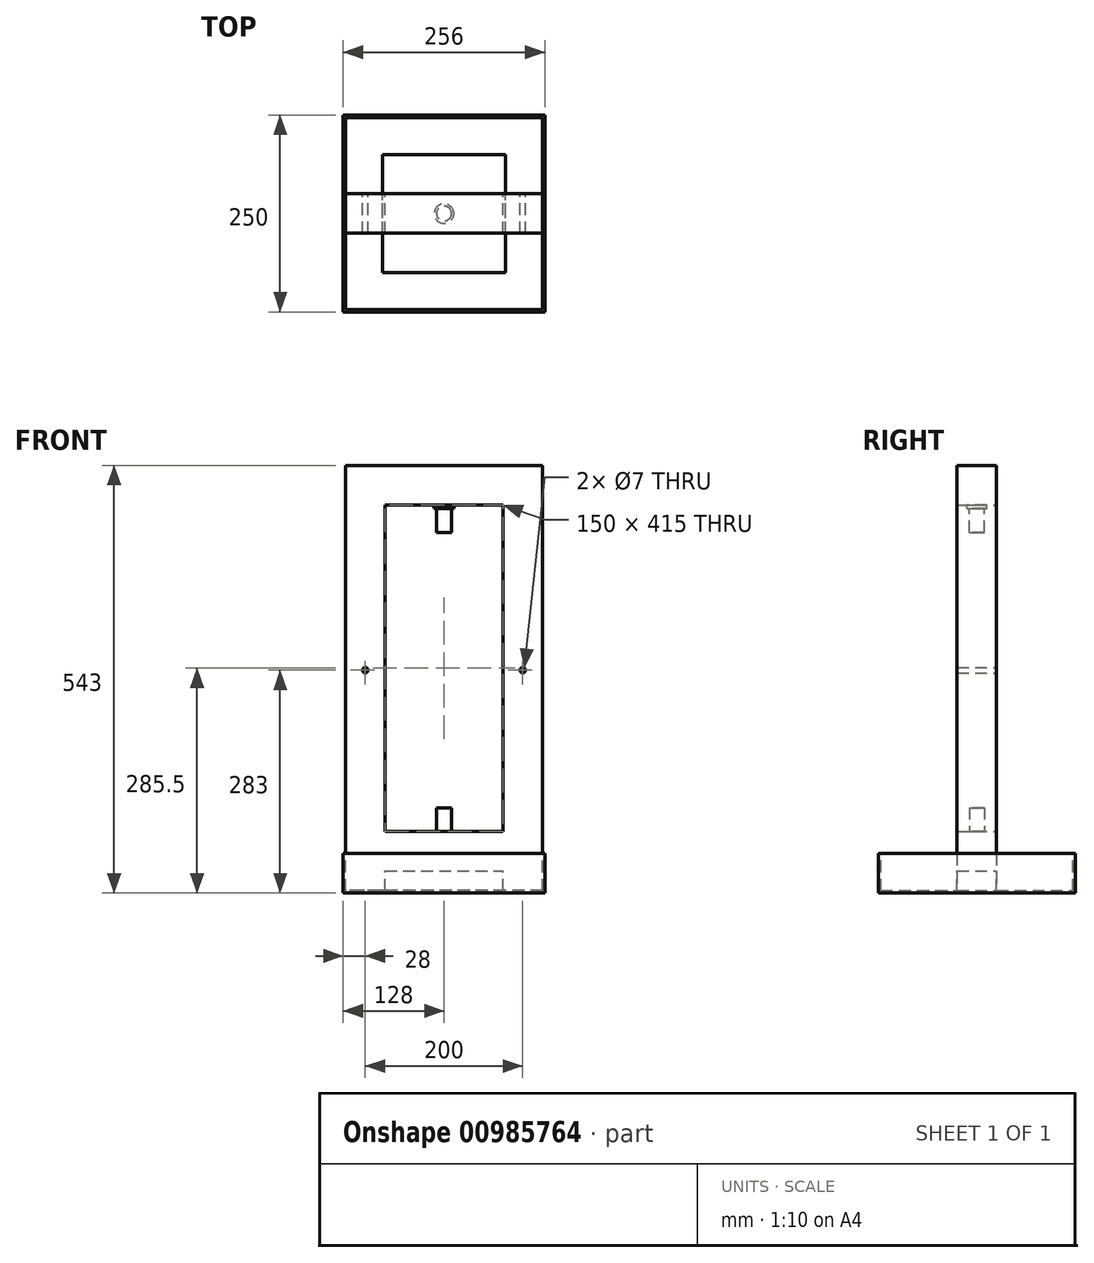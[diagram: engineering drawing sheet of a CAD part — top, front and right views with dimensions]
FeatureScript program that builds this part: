
annotation { "Feature Type Name" : "Feature", "Feature Type Description" : "" }
export const myFeature = defineFeature(function(context is Context, id is Id, definition is map)
    precondition{}
    {
        {
            var Q0;
            Q0=qCreatedBy(makeId("Front.planeOp"),FACE);
            var sketch = newSketch(context, id + "F0", { "sketchPlane" : qUnion([Q0])});
            skLineSegment(sketch, "E0.bottom", {"start": v(125, 0) * mm, "end": v(-125, 0) * mm});
            skLineSegment(sketch, "E0.top", {"start": v(125, -540) * mm, "end": v(75, -540) * mm});
            skLineSegment(sketch, "E0.left", {"start": v(125, 0) * mm, "end": v(125, -540) * mm});
            skLineSegment(sketch, "E0.right", {"start": v(-125, 0) * mm, "end": v(-125, -540) * mm});
            skPoint(sketch, "E0.middle", {"position": v(0, -270) * mm});
            skLineSegment(sketch, "E1.top", {"start": v(75, -50) * mm, "end": v(-75, -50) * mm});
            skLineSegment(sketch, "E1.left", {"start": v(75, -540) * mm, "end": v(75, -515) * mm});
            skLineSegment(sketch, "E1.right", {"start": v(-75, -540) * mm, "end": v(-75, -515) * mm});
            skPoint(sketch, "E1.middle", {"position": v(0, -295) * mm});
            skLineSegment(sketch, "E2.trimOffspring", {"start": v(-75, -540) * mm, "end": v(-125, -540) * mm});
            skLineSegment(sketch, "E3.bottom", {"start": v(-75, -515) * mm, "end": v(75, -515) * mm});
            skLineSegment(sketch, "E3.top", {"start": v(-75, -465) * mm, "end": v(75, -465) * mm});
            skLineSegment(sketch, "E4.trimOffspring", {"start": v(75, -465) * mm, "end": v(75, -50) * mm});
            skLineSegment(sketch, "E5.trimOffspring", {"start": v(-75, -465) * mm, "end": v(-75, -50) * mm});
            skSolve(sketch);
        }
        {
            var Q0;
            Q0=makeQuery(id+"F0.imprint","IMPRINT",FACE,{"disambiguationData":[TD([[makeQuery(id+"F0.imprint","IMPRINT",EDGE,{"derivedFrom":sQuery(id+"F0.wireOp",EDGE,"E0.bottom")}),1.0]])]});
            extrude(context, id + "F1", {"entities" : qUnion([Q0]), "endBound" : BoundingType.SYMMETRIC, "depth" : 50 * mm, "offsetDistance" : 25 * mm});
        }
        {
            var Q0;
            Q0=qCreatedBy(makeId("Front.planeOp"),FACE);
            var sketch = newSketch(context, id + "F2", { "sketchPlane" : qUnion([Q0])});
            skLineSegment(sketch, "E6", {"start": v(-128, -493) * mm, "end": v(-128, -543) * mm});
            skLineSegment(sketch, "E7", {"start": v(-128, -543) * mm, "end": v(-78, -543) * mm});
            skLineSegment(sketch, "E8", {"start": v(-78, -543) * mm, "end": v(-78, -540) * mm});
            skLineSegment(sketch, "E9", {"start": v(-78, -540) * mm, "end": v(-125, -540) * mm});
            skLineSegment(sketch, "E10", {"start": v(-125, -540) * mm, "end": v(-125, -493) * mm});
            skLineSegment(sketch, "E11", {"start": v(-125, -493) * mm, "end": v(-128, -493) * mm});
            skLineSegment(sketch, "E12.MirrorCS", {"start": v(78, -543) * mm, "end": v(78, -540) * mm});
            skLineSegment(sketch, "E13.MirrorCS", {"start": v(125, -493) * mm, "end": v(128, -493) * mm});
            skLineSegment(sketch, "E14.MirrorCS", {"start": v(128, -493) * mm, "end": v(128, -543) * mm});
            skLineSegment(sketch, "E15.MirrorCS", {"start": v(128, -543) * mm, "end": v(78, -543) * mm});
            skLineSegment(sketch, "E16.MirrorCS", {"start": v(125, -540) * mm, "end": v(125, -493) * mm});
            skLineSegment(sketch, "E17.MirrorCS", {"start": v(78, -540) * mm, "end": v(125, -540) * mm});
            skSolve(sketch);
        }
        {
            var Q0;
            Q0=makeQuery(id+"F2.imprint","IMPRINT",FACE,{"disambiguationData":[TD([[makeQuery(id+"F2.imprint","IMPRINT",EDGE,{"derivedFrom":sQuery(id+"F2.wireOp",EDGE,"E6")}),1.0]])]});
            var Q1;
            Q1=makeQuery(id+"F2.imprint","IMPRINT",FACE,{"disambiguationData":[TD([[makeQuery(id+"F2.imprint","IMPRINT",EDGE,{"derivedFrom":sQuery(id+"F2.wireOp",EDGE,"E12.MirrorCS")}),-1.0]])]});
            extrude(context, id + "F3", {"entities" : qUnion([Q0, Q1]), "operationType" : NewBodyOperationType.ADD, "endBound" : BoundingType.SYMMETRIC, "depth" : 250 * mm, "offsetDistance" : 25 * mm});
        }
        {
            var Q0;
            Q0=qCreatedBy(makeId("Right.planeOp"),FACE);
            var sketch = newSketch(context, id + "F4", { "sketchPlane" : qUnion([Q0])});
            skLineSegment(sketch, "E18", {"start": v(125, -493) * mm, "end": v(125, -543) * mm});
            skLineSegment(sketch, "E19", {"start": v(125, -543) * mm, "end": v(75, -543) * mm});
            skLineSegment(sketch, "E20", {"start": v(75, -543) * mm, "end": v(75, -540) * mm});
            skLineSegment(sketch, "E21", {"start": v(75, -540) * mm, "end": v(122, -540) * mm});
            skLineSegment(sketch, "E22", {"start": v(122, -540) * mm, "end": v(122, -493) * mm});
            skLineSegment(sketch, "E23", {"start": v(122, -493) * mm, "end": v(125, -493) * mm});
            skLineSegment(sketch, "E24.MirrorCS", {"start": v(-122, -493) * mm, "end": v(-125, -493) * mm});
            skLineSegment(sketch, "E25.MirrorCS", {"start": v(-75, -543) * mm, "end": v(-75, -540) * mm});
            skLineSegment(sketch, "E26.MirrorCS", {"start": v(-125, -543) * mm, "end": v(-75, -543) * mm});
            skLineSegment(sketch, "E27.MirrorCS", {"start": v(-75, -540) * mm, "end": v(-122, -540) * mm});
            skLineSegment(sketch, "E28.MirrorCS", {"start": v(-122, -540) * mm, "end": v(-122, -493) * mm});
            skLineSegment(sketch, "E29.MirrorCS", {"start": v(-125, -493) * mm, "end": v(-125, -543) * mm});
            skSolve(sketch);
        }
        {
            var Q0;
            Q0=makeQuery(id+"F4.imprint","IMPRINT",FACE,{"disambiguationData":[TD([[makeQuery(id+"F4.imprint","IMPRINT",EDGE,{"derivedFrom":sQuery(id+"F4.wireOp",EDGE,"E18")}),-1.0]])]});
            var Q1;
            Q1=makeQuery(id+"F4.imprint","IMPRINT",FACE,{"disambiguationData":[TD([[makeQuery(id+"F4.imprint","IMPRINT",EDGE,{"derivedFrom":sQuery(id+"F4.wireOp",EDGE,"E24.MirrorCS")}),1.0]])]});
            extrude(context, id + "F5", {"entities" : qUnion([Q0, Q1]), "operationType" : NewBodyOperationType.ADD, "endBound" : BoundingType.SYMMETRIC, "depth" : 250 * mm, "offsetDistance" : 25 * mm});
        }
        {
            var Q0;
            Q0=makeQuery(id+"F1.opExtrude","SWEPT_FACE",FACE,{"disambiguationData":[OSD([sQuery(id+"F0.wireOp",EDGE,"E1.top")])]});
            var sketch = newSketch(context, id + "F6", { "sketchPlane" : qUnion([Q0])});
            skCircle(sketch, "E30", {"center": v(0, 0) * mm, "radius": 9.5 * mm});
            skSolve(sketch);
        }
        {
            var Q0;
            Q0 = qSketchRegion(id + "F6", true);
            extrude(context, id + "F7", {"entities" : qUnion([Q0]), "operationType" : NewBodyOperationType.ADD, "depth" : 35 * mm, "offsetDistance" : 25 * mm});
        }
        {
            var Q0;
            Q0=makeQuery(id+"F1.opExtrude","SWEPT_FACE",FACE,{"disambiguationData":[OSD([sQuery(id+"F0.wireOp",EDGE,"E1.top")])]});
            var sketch = newSketch(context, id + "F8", { "sketchPlane" : qUnion([Q0])});
            skCircle(sketch, "E31", {"center": v(0, 0) * mm, "radius": 12.5 * mm});
            skSolve(sketch);
        }
        {
            var Q0;
            Q0 = qSketchRegion(id + "F8", true);
            extrude(context, id + "F9", {"entities" : qUnion([Q0]), "operationType" : NewBodyOperationType.ADD, "depth" : 5 * mm, "offsetDistance" : 25 * mm});
        }
        {
            var Q0;
            Q0=makeQuery(id+"F1.opExtrude","SWEPT_FACE",FACE,{"disambiguationData":[OSD([sQuery(id+"F0.wireOp",EDGE,"E3.top")])]});
            var sketch = newSketch(context, id + "F10", { "sketchPlane" : qUnion([Q0])});
            skCircle(sketch, "E32", {"center": v(0, 0) * mm, "radius": 9.5 * mm});
            skSolve(sketch);
        }
        {
            var Q0;
            Q0=makeQuery(id+"F10.imprint","IMPRINT",FACE,{"disambiguationData":[TD([[makeQuery(id+"F10.imprint","IMPRINT",EDGE,{"derivedFrom":sQuery(id+"F10.wireOp",EDGE,"E32")}),1.0]])]});
            extrude(context, id + "F11", {"entities" : qUnion([Q0]), "operationType" : NewBodyOperationType.ADD, "depth" : 30 * mm, "offsetDistance" : 25 * mm});
        }
        {
            var Q0;
            Q0=qCreatedBy(makeId("Front.planeOp"),FACE);
            var sketch = newSketch(context, id + "F12", { "sketchPlane" : qUnion([Q0])});
            skCircle(sketch, "E33", {"center": v(-100, -260) * mm, "radius": 3.5 * mm});
            skCircle(sketch, "E34.MirrorC", {"center": v(100, -260) * mm, "radius": 3.5 * mm});
            skSolve(sketch);
        }
        {
            var Q0;
            Q0 = qSketchRegion(id + "F12", true);
            extrude(context, id + "F13", {"entities" : qUnion([Q0]), "operationType" : NewBodyOperationType.REMOVE, "endBound" : BoundingType.SYMMETRIC, "depth" : 60 * mm, "offsetDistance" : 25 * mm});
        }
    });
